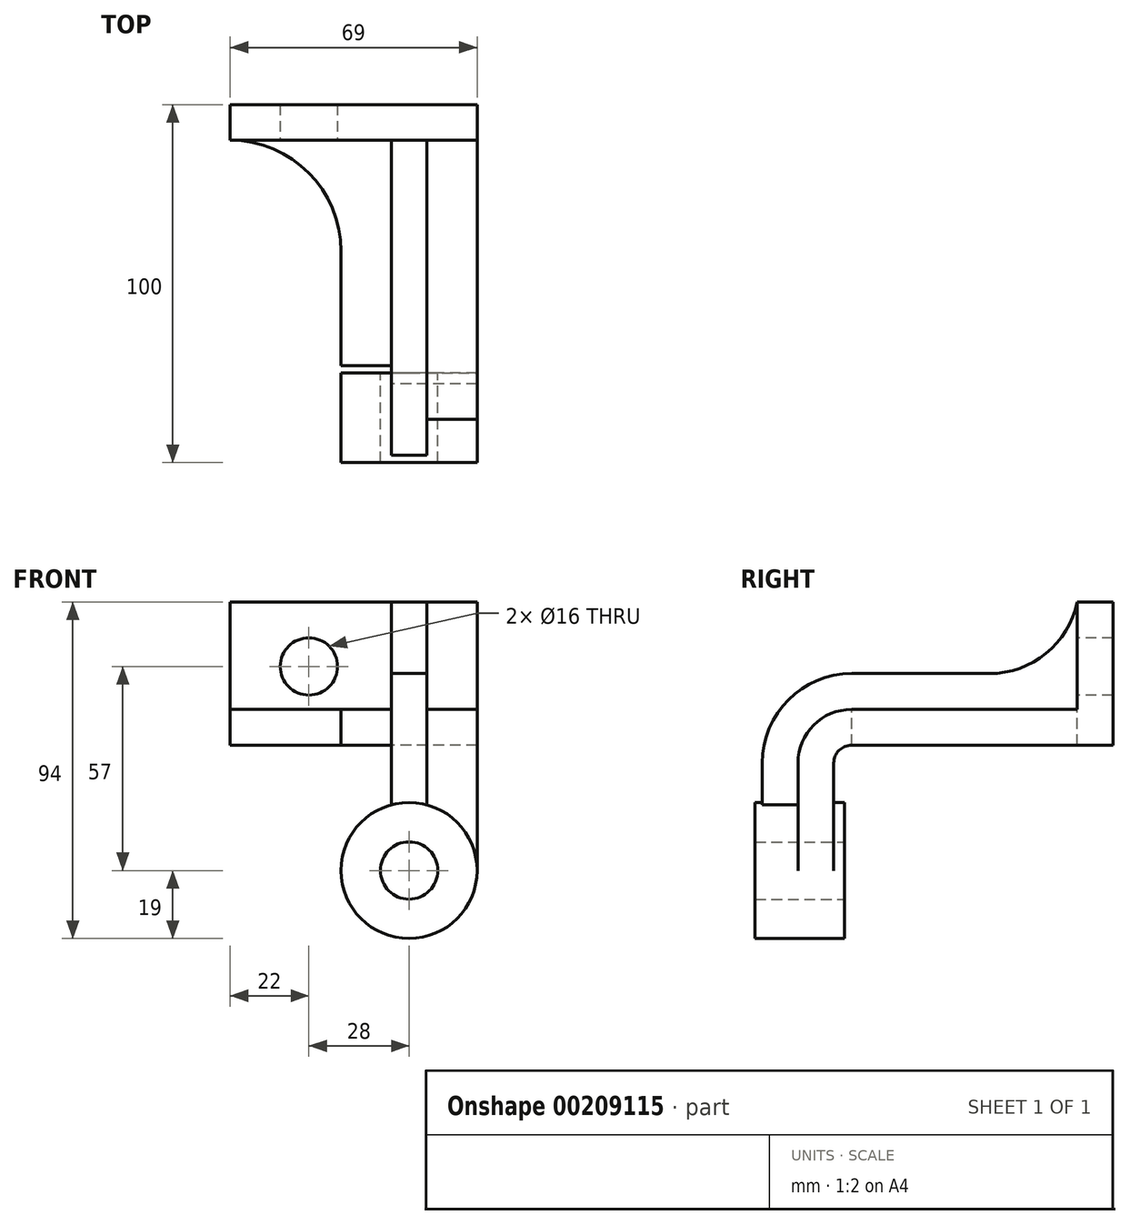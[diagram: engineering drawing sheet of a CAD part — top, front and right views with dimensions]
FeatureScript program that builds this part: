
annotation { "Feature Type Name" : "Feature", "Feature Type Description" : "" }
export const myFeature = defineFeature(function(context is Context, id is Id, definition is map)
    precondition{}
    {
        {
            var Q0;
            Q0=qCreatedBy(makeId("Right.planeOp"),FACE);
            var sketch = newSketch(context, id + "F0", { "sketchPlane" : qUnion([Q0])});
            skLineSegment(sketch, "E0", {"start": v(10, 0) * mm, "end": v(10, 30) * mm});
            skLineSegment(sketch, "E1", {"start": v(15, 35) * mm, "end": v(88, 35) * mm});
            skLineSegment(sketch, "E2", {"start": v(88, 35) * mm, "end": v(88, 75) * mm});
            skLineSegment(sketch, "E3", {"start": v(88, 75) * mm, "end": v(78, 75) * mm});
            skLineSegment(sketch, "E4", {"start": v(78, 75) * mm, "end": v(78, 45) * mm});
            skLineSegment(sketch, "E5", {"start": v(78, 45) * mm, "end": v(15, 45) * mm});
            skLineSegment(sketch, "E6", {"start": v(0, 30) * mm, "end": v(0, 0) * mm});
            skLineSegment(sketch, "E7", {"start": v(0, 0) * mm, "end": v(10, 0) * mm});
            skLineSegment(sketch, "E8", {"start": v(0, 0) * mm, "end": v(-10, 0) * mm});
            skLineSegment(sketch, "E9", {"start": v(-10, 0) * mm, "end": v(-10, 30) * mm});
            skLineSegment(sketch, "E10", {"start": v(15, 55) * mm, "end": v(53.5, 55) * mm});
            skArc(sketch, "E11", {"start": v(53.5, 55) * mm, "mid": v(69.32, 60.64) * mm, "end": v(78, 75) * mm});
            skPoint(sketch, "E12.visualSharp", {"position": v(10, 35) * mm});
            skArc(sketch, "E12.filletArc", {"start": v(15, 35) * mm, "mid": v(11.46, 33.54) * mm, "end": v(10, 30) * mm});
            skPoint(sketch, "E13.visualSharp", {"position": v(0, 45) * mm});
            skArc(sketch, "E13.filletArc", {"start": v(15, 45) * mm, "mid": v(4.4, 40.6) * mm, "end": v(0, 30) * mm});
            skPoint(sketch, "E14.visualSharp", {"position": v(-10, 55) * mm});
            skArc(sketch, "E14.filletArc", {"start": v(15, 55) * mm, "mid": v(-2.68, 47.68) * mm, "end": v(-10, 30) * mm});
            skSolve(sketch);
        }
        {
            var Q0;
            Q0=makeQuery(id+"F0.imprint","IMPRINT",FACE,{"disambiguationData":[TD([[makeQuery(id+"F0.imprint","IMPRINT",EDGE,{"derivedFrom":sQuery(id+"F0.wireOp",EDGE,"E0")}),1.0]])]});
            extrude(context, id + "F1", {"entities" : qUnion([Q0]), "endBound" : BoundingType.SYMMETRIC, "depth" : 38 * mm});
        }
        {
            var Q0;
            Q0=makeQuery(id+"F0.imprint","IMPRINT",FACE,{"disambiguationData":[TD([[makeQuery(id+"F0.imprint","IMPRINT",EDGE,{"derivedFrom":sQuery(id+"F0.wireOp",EDGE,"E4")}),-1.0]])]});
            extrude(context, id + "F2", {"entities" : qUnion([Q0]), "operationType" : NewBodyOperationType.ADD, "endBound" : BoundingType.SYMMETRIC, "depth" : 10 * mm});
        }
        {
            var Q0;
            Q0=makeQuery(id+"F0.imprint","IMPRINT",FACE,{"disambiguationData":[TD([[makeQuery(id+"F0.imprint","IMPRINT",EDGE,{"derivedFrom":sQuery(id+"F0.wireOp",EDGE,"E0")}),1.0]])]});
            extrude(context, id + "F3", {"entities" : qUnion([Q0]), "operationType" : NewBodyOperationType.ADD, "oppositeDirection" : true, "depth" : 50 * mm});
        }
        {
            var Q0;
            {var subQ0=sQuery(id+"F0.wireOp",EDGE,"E5");var subQ1=sQuery(id+"F0.wireOp",EDGE,"E6");var subQ2=sQuery(id+"F0.wireOp",EDGE,"E4");Q0=makeQuery(id+"F3.boolean.opBoolean","MERGE",FACE,{"derivedFrom":[makeQuery(id+"F2.boolean.opBoolean","SPLIT",FACE,{"disambiguationData":[TD([makeQuery(id+"F2.opExtrude","CAP_FACE",FACE,{"disambiguationData":[OSD([subQ2,subQ0,subQ1,sQuery(id+"F0.wireOp",EDGE,"E8"),sQuery(id+"F0.wireOp",EDGE,"E9"),sQuery(id+"F0.wireOp",EDGE,"E10"),sQuery(id+"F0.wireOp",EDGE,"E11")])],"isStart":true})])],"derivedFrom":makeQuery(id+"F1.opExtrude","SWEPT_FACE",FACE,{"disambiguationData":[OSD([subQ0])]})}),makeQuery(id+"F3.opExtrude","SWEPT_FACE",FACE,{"disambiguationData":[OSD([subQ0])]})]});}
            var sketch = newSketch(context, id + "F4", { "sketchPlane" : qUnion([Q0])});
            skLineSegment(sketch, "E15.0", {"start": v(-5, 78) * mm, "end": v(-50, 78) * mm});
            skLineSegment(sketch, "E15.1", {"start": v(-5, 78) * mm, "end": v(-5, 78) * mm});
            skLineSegment(sketch, "E15.3", {"start": v(-50, 78) * mm, "end": v(-50, 78) * mm});
            skArc(sketch, "E16", {"start": v(-19, 47) * mm, "mid": v(-28.08, 68.92) * mm, "end": v(-50, 78) * mm});
            skLineSegment(sketch, "E17", {"start": v(-19, 47) * mm, "end": v(-19, 15) * mm});
            skPoint(sketch, "E17.endSnap0", {"position": v(-27.5, 15) * mm});
            skLineSegment(sketch, "E18", {"start": v(-5, 15) * mm, "end": v(-5, 78) * mm});
            skLineSegment(sketch, "E19.0", {"start": v(-5, 0) * mm, "end": v(-50, 0) * mm});
            skLineSegment(sketch, "E20", {"start": v(-19, 15) * mm, "end": v(-19, 0) * mm});
            skLineSegment(sketch, "E21", {"start": v(-19, 0) * mm, "end": v(-5, 0) * mm});
            skLineSegment(sketch, "E22", {"start": v(-5, 0) * mm, "end": v(-5, 15) * mm});
            skLineSegment(sketch, "E23", {"start": v(-50, 0) * mm, "end": v(-50, 78) * mm});
            skSolve(sketch);
        }
        {
            var Q0;
            Q0=makeQuery(id+"F4.imprint","IMPRINT",FACE,{"disambiguationData":[TD([[makeQuery(id+"F4.imprint","IMPRINT",EDGE,{"derivedFrom":sQuery(id+"F4.wireOp",EDGE,"E16")}),1.0]])]});
            var Q1;
            {var subQ0=sQuery(id+"F4.wireOp",EDGE,"E19.0");Q1=makeQuery(id+"F4.imprint","IMPRINT",FACE,{"disambiguationData":[TD([[makeQuery(id+"F4.imprint","IMPRINT",EDGE,{"derivedFrom":subQ0}),-1.0]])]});}
            extrude(context, id + "F5", {"entities" : qUnion([Q0, Q1]), "operationType" : NewBodyOperationType.REMOVE, "endBound" : BoundingType.THROUGH_ALL, "oppositeDirection" : true, "depth" : 25 * mm});
        }
        {
            var Q0;
            Q0=qCreatedBy(makeId("Front.planeOp"),FACE);
            var sketch = newSketch(context, id + "F6", { "sketchPlane" : qUnion([Q0])});
            skCircle(sketch, "E24", {"center": v(0, 0) * mm, "radius": 19 * mm});
            skCircle(sketch, "E25", {"center": v(0, 0) * mm, "radius": 8 * mm});
            skSolve(sketch);
        }
        {
            var Q0;
            Q0=makeQuery(id+"F6.imprint","IMPRINT",FACE,{"disambiguationData":[TD([[makeQuery(id+"F6.imprint","IMPRINT",EDGE,{"derivedFrom":sQuery(id+"F6.wireOp",EDGE,"E24")}),1.0]])]});
            var Q1;
            Q1=makeQuery(id+"F6.imprint","IMPRINT",FACE,{"disambiguationData":[TD([[makeQuery(id+"F6.imprint","IMPRINT",EDGE,{"derivedFrom":sQuery(id+"F6.wireOp",EDGE,"E25")}),1.0]])]});
            extrude(context, id + "F7", {"entities" : qUnion([Q0, Q1]), "operationType" : NewBodyOperationType.ADD, "depth" : 12 * mm});
        }
        {
            var Q0;
            Q0=makeQuery(id+"F6.imprint","IMPRINT",FACE,{"disambiguationData":[TD([[makeQuery(id+"F6.imprint","IMPRINT",EDGE,{"derivedFrom":sQuery(id+"F6.wireOp",EDGE,"E24")}),1.0]])]});
            var Q1;
            Q1=makeQuery(id+"F6.imprint","IMPRINT",FACE,{"disambiguationData":[TD([[makeQuery(id+"F6.imprint","IMPRINT",EDGE,{"derivedFrom":sQuery(id+"F6.wireOp",EDGE,"E25")}),1.0]])]});
            extrude(context, id + "F8", {"entities" : qUnion([Q0, Q1]), "operationType" : NewBodyOperationType.ADD, "oppositeDirection" : true, "depth" : 13 * mm});
        }
        {
            var Q0;
            Q0=makeQuery(id+"F6.imprint","IMPRINT",FACE,{"disambiguationData":[TD([[makeQuery(id+"F6.imprint","IMPRINT",EDGE,{"derivedFrom":sQuery(id+"F6.wireOp",EDGE,"E25")}),1.0]])]});
            extrude(context, id + "F9", {"entities" : qUnion([Q0]), "operationType" : NewBodyOperationType.REMOVE, "endBound" : BoundingType.SYMMETRIC, "depth" : 100 * mm});
        }
        {
            var Q0;
            {var subQ0=sQuery(id+"F0.wireOp",EDGE,"E4");var subQ1=sQuery(id+"F0.wireOp",EDGE,"E5");var subQ2=sQuery(id+"F0.wireOp",EDGE,"E13.filletArc");var subQ3=sQuery(id+"F0.wireOp",EDGE,"E11");var subQ4=sQuery(id+"F0.wireOp",EDGE,"E6");Q0=makeQuery(id+"F3.boolean.opBoolean","MERGE",FACE,{"derivedFrom":[makeQuery(id+"F2.boolean.opBoolean","SPLIT",FACE,{"disambiguationData":[TD([makeQuery(id+"F2.opExtrude","CAP_FACE",FACE,{"disambiguationData":[OSD([subQ0,subQ1,subQ4,sQuery(id+"F0.wireOp",EDGE,"E8"),sQuery(id+"F0.wireOp",EDGE,"E9"),sQuery(id+"F0.wireOp",EDGE,"E10"),subQ3,subQ2,sQuery(id+"F0.wireOp",EDGE,"E14.filletArc")])],"isStart":true})])],"derivedFrom":makeQuery(id+"F1.opExtrude","SWEPT_FACE",FACE,{"disambiguationData":[OSD([subQ0])]})}),makeQuery(id+"F3.opExtrude","SWEPT_FACE",FACE,{"disambiguationData":[OSD([subQ0])]})]});}
            var sketch = newSketch(context, id + "F10", { "sketchPlane" : qUnion([Q0])});
            skCircle(sketch, "E26", {"center": v(-28, 57) * mm, "radius": 8 * mm});
            skSolve(sketch);
        }
        {
            var Q0;
            Q0=makeQuery(id+"F10.imprint","IMPRINT",FACE,{"disambiguationData":[TD([[makeQuery(id+"F10.imprint","IMPRINT",EDGE,{"derivedFrom":sQuery(id+"F10.wireOp",EDGE,"E26")}),1.0]])]});
            extrude(context, id + "F11", {"entities" : qUnion([Q0]), "operationType" : NewBodyOperationType.REMOVE, "endBound" : BoundingType.THROUGH_ALL, "oppositeDirection" : true, "depth" : 25 * mm});
        }
    });
